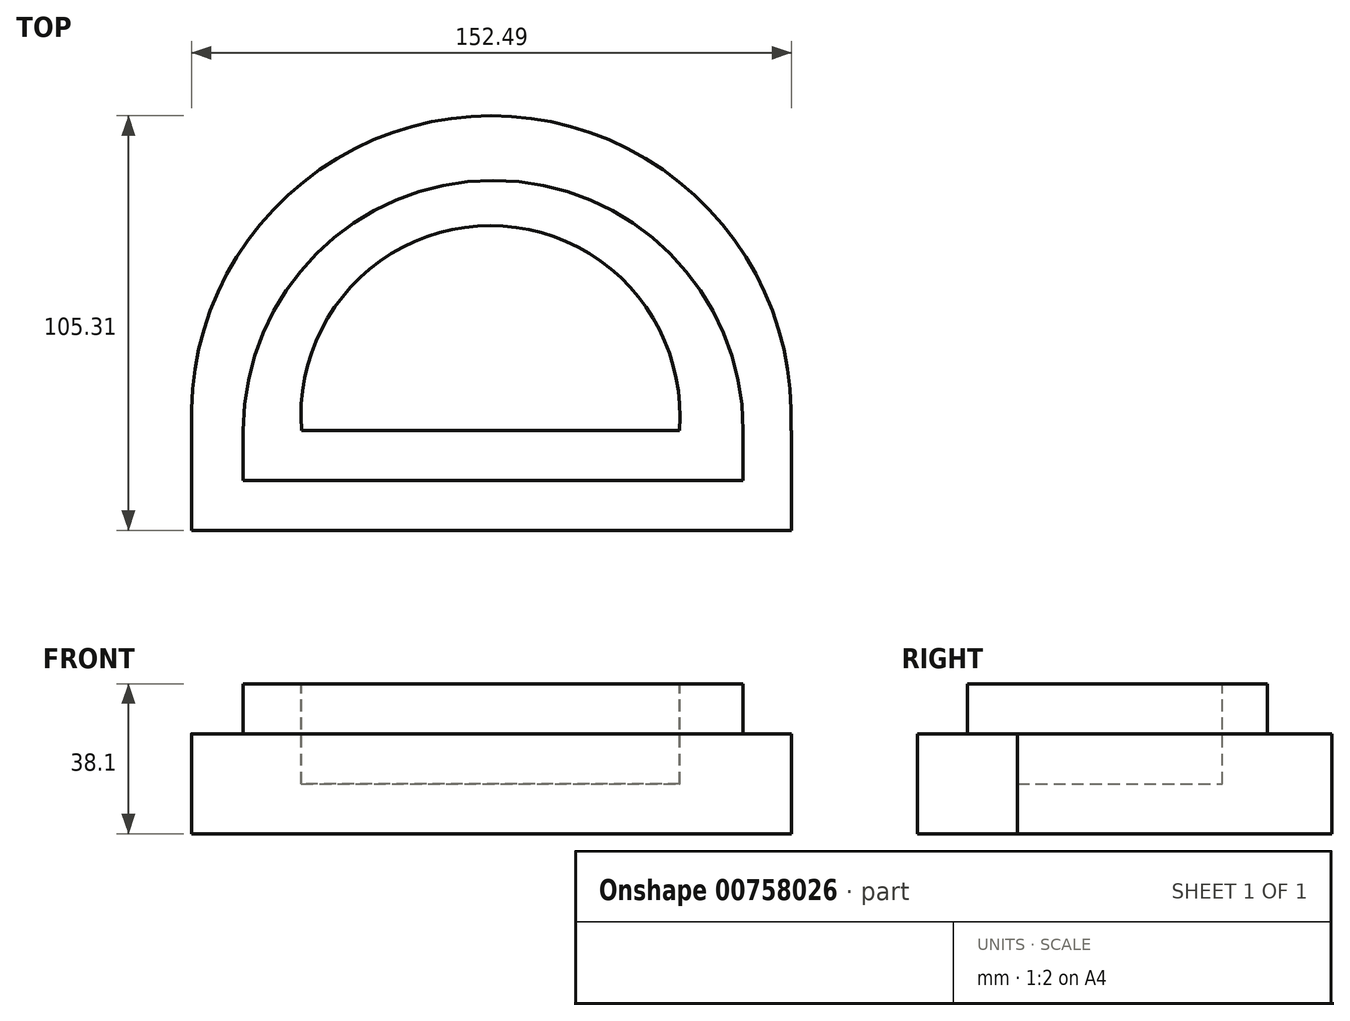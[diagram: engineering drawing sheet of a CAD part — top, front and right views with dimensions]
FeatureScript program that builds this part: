
annotation { "Feature Type Name" : "Feature", "Feature Type Description" : "" }
export const myFeature = defineFeature(function(context is Context, id is Id, definition is map)
    precondition{}
    {
        {
            var Q0;
            Q0=qCreatedBy(makeId("Top.planeOp"),FACE);
            var sketch = newSketch(context, id + "F0", { "sketchPlane" : qUnion([Q0])});
            skArc(sketch, "E0", {"start": v(75.6, 0) * mm, "mid": v(-0.5, 79.9) * mm, "end": v(-76.61, 0) * mm});
            skLineSegment(sketch, "E1.bottom", {"start": v(-76.61, 0) * mm, "end": v(75.79, 0) * mm});
            skLineSegment(sketch, "E1.top", {"start": v(-76.61, -25.4) * mm, "end": v(75.79, -25.4) * mm});
            skLineSegment(sketch, "E1.left", {"start": v(-76.61, 0) * mm, "end": v(-76.61, -25.4) * mm});
            skLineSegment(sketch, "E1.right", {"start": v(75.79, 0) * mm, "end": v(75.79, -25.4) * mm});
            skSolve(sketch);
        }
        {
            var Q0;
            {var subQ0=sQuery(id+"F0.wireOp",EDGE,"E0");Q0=makeQuery(id+"F0.imprint","IMPRINT",FACE,{"disambiguationData":[TD([[makeQuery(id+"F0.imprint","IMPRINT",EDGE,{"derivedFrom":subQ0}),1.0]])]});}
            var Q1;
            Q1=makeQuery(id+"F0.imprint","IMPRINT",FACE,{"disambiguationData":[TD([[makeQuery(id+"F0.imprint","IMPRINT",EDGE,{"derivedFrom":sQuery(id+"F0.wireOp",EDGE,"E1.top")}),1.0]])]});
            extrude(context, id + "F1", {"entities" : qUnion([Q0, Q1]), "depth" : 25.4 * mm, "offsetDistance" : 25.4 * mm});
        }
        {
            var Q0;
            Q0=makeQuery(id+"F1.opExtrude","CAP_FACE",FACE,{"disambiguationData":[OSD([sQuery(id+"F0.wireOp",EDGE,"E0"),sQuery(id+"F0.wireOp",EDGE,"E1.bottom"),sQuery(id+"F0.wireOp",EDGE,"E1.top"),sQuery(id+"F0.wireOp",EDGE,"E1.left"),sQuery(id+"F0.wireOp",EDGE,"E1.right")])],"isStart":false});
            var sketch = newSketch(context, id + "F2", { "sketchPlane" : qUnion([Q0])});
            skArc(sketch, "E2", {"start": v(63.5, 0) * mm, "mid": v(0, 63.5) * mm, "end": v(-63.5, 0) * mm});
            skPoint(sketch, "E3.oppositeSnap0", {"position": v(-76.61, -12.7) * mm});
            skLineSegment(sketch, "E3.bottom", {"start": v(-63.5, 0) * mm, "end": v(63.5, 0) * mm});
            skLineSegment(sketch, "E3.top", {"start": v(-63.5, -12.7) * mm, "end": v(63.5, -12.7) * mm});
            skLineSegment(sketch, "E3.left", {"start": v(-63.5, 0) * mm, "end": v(-63.5, -12.7) * mm});
            skLineSegment(sketch, "E3.right", {"start": v(63.5, 0) * mm, "end": v(63.5, -12.7) * mm});
            skSolve(sketch);
        }
        {
            var Q0;
            Q0=makeQuery(id+"F2.imprint","IMPRINT",FACE,{"disambiguationData":[TD([[makeQuery(id+"F2.imprint","IMPRINT",EDGE,{"derivedFrom":sQuery(id+"F2.wireOp",EDGE,"E2")}),1.0]])]});
            var Q1;
            Q1=makeQuery(id+"F2.imprint","IMPRINT",FACE,{"disambiguationData":[TD([[makeQuery(id+"F2.imprint","IMPRINT",EDGE,{"derivedFrom":sQuery(id+"F2.wireOp",EDGE,"E3.bottom")}),-1.0]])]});
            extrude(context, id + "F3", {"entities" : qUnion([Q0, Q1]), "operationType" : NewBodyOperationType.ADD, "depth" : 12.7 * mm, "offsetDistance" : 25.4 * mm});
        }
        {
            var Q0;
            Q0=makeQuery(id+"F3.opExtrude","CAP_FACE",FACE,{"disambiguationData":[OSD([sQuery(id+"F2.wireOp",EDGE,"E2"),sQuery(id+"F2.wireOp",EDGE,"E3.top"),sQuery(id+"F2.wireOp",EDGE,"E3.left"),sQuery(id+"F2.wireOp",EDGE,"E3.right")])],"isStart":false});
            var sketch = newSketch(context, id + "F4", { "sketchPlane" : qUnion([Q0])});
            skArc(sketch, "E4", {"start": v(47.26, 0) * mm, "mid": v(-0.73, 51.99) * mm, "end": v(-48.73, 0) * mm});
            skLineSegment(sketch, "E5", {"start": v(-48.73, 0) * mm, "end": v(47.26, 0) * mm});
            skSolve(sketch);
        }
        {
            var Q0;
            Q0=makeQuery(id+"F4.imprint","IMPRINT",FACE,{"disambiguationData":[TD([[makeQuery(id+"F4.imprint","IMPRINT",EDGE,{"derivedFrom":sQuery(id+"F4.wireOp",EDGE,"E4")}),1.0]])]});
            extrude(context, id + "F5", {"entities" : qUnion([Q0]), "operationType" : NewBodyOperationType.REMOVE, "oppositeDirection" : true, "depth" : 25.4 * mm, "offsetDistance" : 25.4 * mm});
        }
    });
